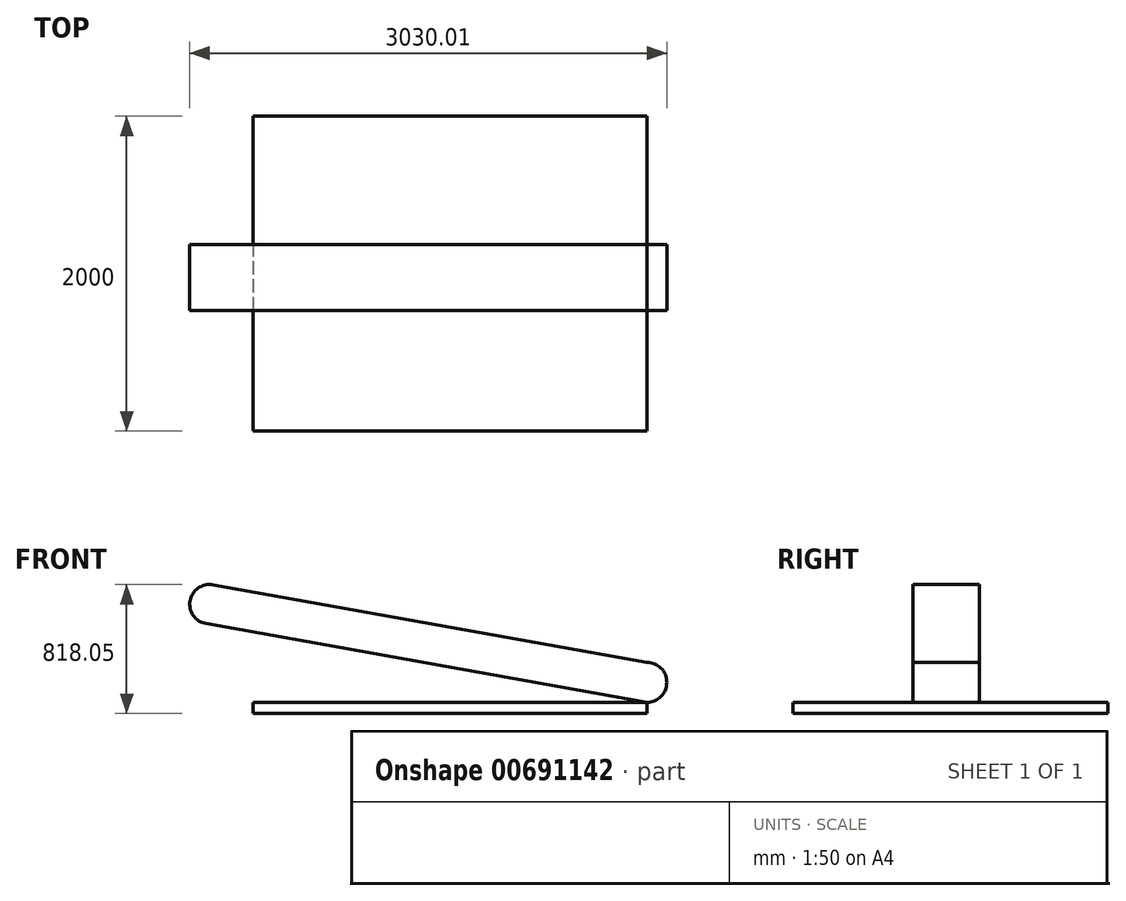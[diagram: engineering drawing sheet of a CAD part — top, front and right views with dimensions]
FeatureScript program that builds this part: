
annotation { "Feature Type Name" : "Feature", "Feature Type Description" : "" }
export const myFeature = defineFeature(function(context is Context, id is Id, definition is map)
    precondition{}
    {
        {
            var Q0;
            Q0=qCreatedBy(makeId("Top.planeOp"),FACE);
            var sketch = newSketch(context, id + "F0", { "sketchPlane" : qUnion([Q0])});
            skLineSegment(sketch, "E0.bottom", {"start": v(-1250, 1025.77) * mm, "end": v(1250, 1025.77) * mm});
            skLineSegment(sketch, "E0.top", {"start": v(-1250, -974.23) * mm, "end": v(1250, -974.23) * mm});
            skLineSegment(sketch, "E0.left", {"start": v(-1250, 1025.77) * mm, "end": v(-1250, -974.23) * mm});
            skLineSegment(sketch, "E0.right", {"start": v(1250, 1025.77) * mm, "end": v(1250, -974.23) * mm});
            skLineSegment(sketch, "E1.bottom", {"start": v(-1250, -210) * mm, "end": v(1250, -210) * mm});
            skLineSegment(sketch, "E1.top", {"start": v(-1250, 210) * mm, "end": v(1250, 210) * mm});
            skLineSegment(sketch, "E1.left", {"start": v(-1250, -210) * mm, "end": v(-1250, 210) * mm});
            skLineSegment(sketch, "E1.right", {"start": v(1250, -210) * mm, "end": v(1250, 210) * mm});
            skLineSegment(sketch, "E2", {"start": v(-1250, 0) * mm, "end": v(1250, 0) * mm, "construction": true});
            skSolve(sketch);
        }
        {
            var Q0;
            {var subQ0=sQuery(id+"F0.wireOp",EDGE,"E0.top");Q0=makeQuery(id+"F0.imprint","IMPRINT",FACE,{"disambiguationData":[TD([[makeQuery(id+"F0.imprint","IMPRINT",EDGE,{"derivedFrom":subQ0}),1.0]])]});}
            var Q1;
            Q1=makeQuery(id+"F0.imprint","IMPRINT",FACE,{"disambiguationData":[TD([[makeQuery(id+"F0.imprint","IMPRINT",EDGE,{"derivedFrom":sQuery(id+"F0.wireOp",EDGE,"E1.bottom")}),1.0]])]});
            var Q2;
            {var subQ0=sQuery(id+"F0.wireOp",EDGE,"E0.bottom");Q2=makeQuery(id+"F0.imprint","IMPRINT",FACE,{"disambiguationData":[TD([[makeQuery(id+"F0.imprint","IMPRINT",EDGE,{"derivedFrom":subQ0}),-1.0]])]});}
            extrude(context, id + "F1", {"entities" : qUnion([Q0, Q1, Q2]), "oppositeDirection" : true, "depth" : 70 * mm, "offsetDistance" : 25 * mm});
        }
        {
            var Q0;
            Q0=qCreatedBy(makeId("Front.planeOp"),FACE);
            var sketch = newSketch(context, id + "F2", { "sketchPlane" : qUnion([Q0])});
            skLineSegment(sketch, "E3", {"start": v(-1550, 500) * mm, "end": v(1250, 0) * mm});
            skPoint(sketch, "E4", {"position": v(-1550, 500) * mm});
            skLineSegment(sketch, "E5", {"start": v(-1250, 0) * mm, "end": v(-1550, 0) * mm, "construction": true});
            skLineSegment(sketch, "E6", {"start": v(-1550, 0) * mm, "end": v(-1550, 500) * mm, "construction": true});
            skLineSegment(sketch, "E7", {"start": v(-1506.05, 746.1) * mm, "end": v(1250, 253.95) * mm});
            skArc(sketch, "E8", {"start": v(-1506.05, 746.1) * mm, "mid": v(-1651.08, 645.03) * mm, "end": v(-1550, 500) * mm});
            skArc(sketch, "E9", {"start": v(1250, 0) * mm, "mid": v(1376.98, 126.98) * mm, "end": v(1250, 253.95) * mm});
            skSolve(sketch);
        }
        {
            var Q0;
            Q0=makeQuery(id+"F2.imprint","IMPRINT",FACE,{"disambiguationData":[TD([[makeQuery(id+"F2.imprint","IMPRINT",EDGE,{"derivedFrom":sQuery(id+"F2.wireOp",EDGE,"E3")}),1.0]])]});
            extrude(context, id + "F3", {"entities" : qUnion([Q0]), "depth" : 420 * mm, "hasOffset" : true, "offsetDistance" : 25 * mm, "hasSecondDirection" : true, "secondDirectionOppositeDirection" : true, "secondDirectionDepth" : 25 * mm, "symmetric" : true});
        }
    });
